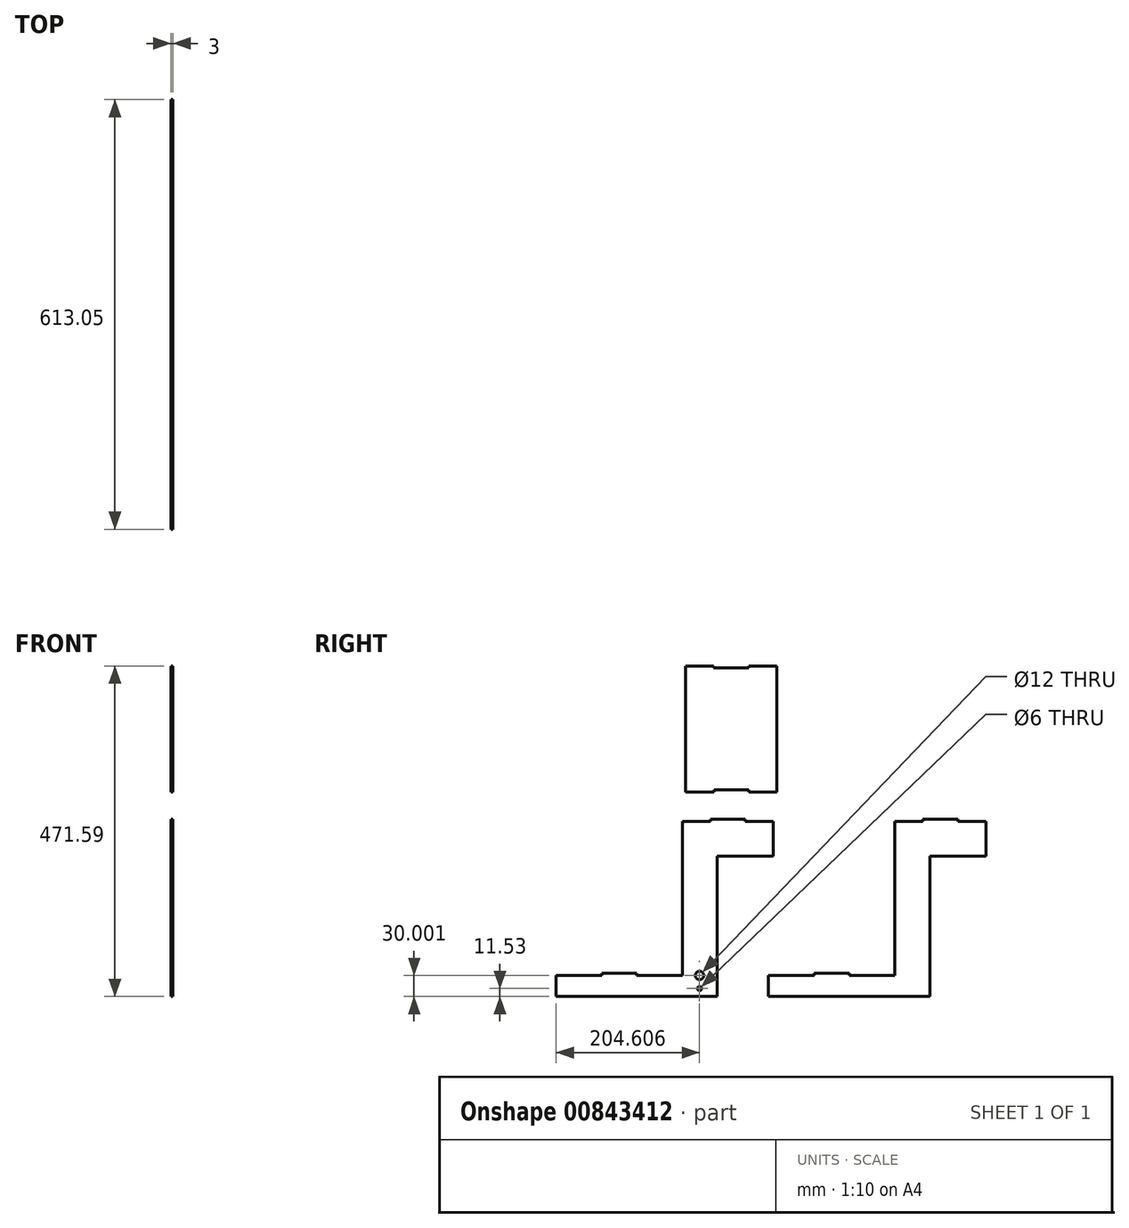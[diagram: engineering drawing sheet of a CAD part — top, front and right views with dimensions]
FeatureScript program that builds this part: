
annotation { "Feature Type Name" : "Feature", "Feature Type Description" : "" }
export const myFeature = defineFeature(function(context is Context, id is Id, definition is map)
    precondition{}
    {
        {
            var Q0;
            Q0=qCreatedBy(makeId("Right.planeOp"),FACE);
            var sketch = newSketch(context, id + "F0", { "sketchPlane" : qUnion([Q0])});
            skLineSegment(sketch, "E0", {"start": v(0, 42.16) * mm, "end": v(40, 42.16) * mm});
            skLineSegment(sketch, "E1", {"start": v(130, 42.16) * mm, "end": v(130, -7.84) * mm});
            skLineSegment(sketch, "E2", {"start": v(50, -7.84) * mm, "end": v(130, -7.84) * mm});
            skLineSegment(sketch, "E3", {"start": v(50, -7.84) * mm, "end": v(50, -207.84) * mm});
            skLineSegment(sketch, "E4", {"start": v(50, -207.84) * mm, "end": v(-180, -207.84) * mm});
            skLineSegment(sketch, "E5", {"start": v(-180, -207.84) * mm, "end": v(-180, -177.84) * mm});
            skLineSegment(sketch, "E6", {"start": v(0, -177.84) * mm, "end": v(-65, -177.84) * mm});
            skLineSegment(sketch, "E7", {"start": v(0, -177.84) * mm, "end": v(0, 42.16) * mm});
            skLineSegment(sketch, "E8", {"start": v(-298.05, 42.16) * mm, "end": v(-263.05, 42.16) * mm});
            skLineSegment(sketch, "E9", {"start": v(-173.05, 37.16) * mm, "end": v(-173.05, -2.84) * mm});
            skLineSegment(sketch, "E10", {"start": v(-248.05, -7.84) * mm, "end": v(-178.05, -7.84) * mm});
            skLineSegment(sketch, "E11", {"start": v(-253.05, -12.84) * mm, "end": v(-253.05, -207.84) * mm});
            skLineSegment(sketch, "E12", {"start": v(-253.05, -207.84) * mm, "end": v(-483.05, -207.84) * mm});
            skLineSegment(sketch, "E13", {"start": v(-483.05, -207.84) * mm, "end": v(-483.05, -177.84) * mm});
            skLineSegment(sketch, "E14", {"start": v(-303.05, -177.84) * mm, "end": v(-368.05, -177.84) * mm});
            skLineSegment(sketch, "E15", {"start": v(-303.05, -177.84) * mm, "end": v(-303.05, 37.16) * mm});
            skCircle(sketch, "E16", {"center": v(-278.44, -177.84) * mm, "radius": 6 * mm});
            skLineSegment(sketch, "E17.bottom", {"start": v(-298.36, 83.75) * mm, "end": v(-258.01, 83.75) * mm});
            skLineSegment(sketch, "E17.top", {"start": v(-298.36, 263.75) * mm, "end": v(-258.36, 263.75) * mm});
            skLineSegment(sketch, "E17.left", {"start": v(-298.36, 83.75) * mm, "end": v(-298.36, 263.75) * mm});
            skLineSegment(sketch, "E17.right", {"start": v(-168.36, 83.75) * mm, "end": v(-168.36, 263.75) * mm});
            skCircle(sketch, "E18", {"center": v(-278.44, -196.31) * mm, "radius": 3 * mm});
            skLineSegment(sketch, "E19", {"start": v(-263.05, 42.16) * mm, "end": v(-263.05, 45.16) * mm});
            skLineSegment(sketch, "E20", {"start": v(-263.05, 45.16) * mm, "end": v(-213.05, 45.16) * mm});
            skLineSegment(sketch, "E21", {"start": v(-213.05, 45.16) * mm, "end": v(-213.05, 42.16) * mm});
            skLineSegment(sketch, "E22.trimOffspring", {"start": v(-213.05, 42.16) * mm, "end": v(-178.05, 42.16) * mm});
            skLineSegment(sketch, "E23.top", {"start": v(-258.01, 86.75) * mm, "end": v(-208.01, 86.75) * mm});
            skLineSegment(sketch, "E23.left", {"start": v(-258.01, 83.75) * mm, "end": v(-258.01, 86.75) * mm});
            skLineSegment(sketch, "E23.right", {"start": v(-208.01, 83.75) * mm, "end": v(-208.01, 86.75) * mm});
            skLineSegment(sketch, "E24.trimOffspring", {"start": v(-208.01, 83.75) * mm, "end": v(-168.36, 83.75) * mm});
            skPoint(sketch, "E25.visualSharp", {"position": v(-303.05, 42.16) * mm});
            skPoint(sketch, "E26.visualSharp", {"position": v(-173.05, 42.16) * mm});
            skPoint(sketch, "E27.visualSharp", {"position": v(-173.05, -7.84) * mm});
            skPoint(sketch, "E28.visualSharp", {"position": v(-253.05, -7.84) * mm});
            skLineSegment(sketch, "E29", {"start": v(-298.05, 42.16) * mm, "end": v(-303.05, 42.16) * mm});
            skLineSegment(sketch, "E30", {"start": v(-303.05, 42.16) * mm, "end": v(-303.05, 37.16) * mm});
            skLineSegment(sketch, "E31", {"start": v(-173.05, 42.16) * mm, "end": v(-178.05, 42.16) * mm});
            skLineSegment(sketch, "E32", {"start": v(-173.05, 42.16) * mm, "end": v(-173.05, 37.16) * mm});
            skLineSegment(sketch, "E33", {"start": v(-173.05, -2.84) * mm, "end": v(-173.05, -7.84) * mm});
            skLineSegment(sketch, "E34", {"start": v(-173.05, -7.84) * mm, "end": v(-178.05, -7.84) * mm});
            skLineSegment(sketch, "E35", {"start": v(-248.05, -7.84) * mm, "end": v(-253.05, -7.84) * mm});
            skLineSegment(sketch, "E36", {"start": v(-253.05, -12.84) * mm, "end": v(-253.05, -7.84) * mm});
            skLineSegment(sketch, "E37", {"start": v(-483.05, -177.84) * mm, "end": v(-418.05, -177.84) * mm});
            skLineSegment(sketch, "E38", {"start": v(-418.05, -177.84) * mm, "end": v(-418.05, -174.84) * mm});
            skLineSegment(sketch, "E39", {"start": v(-418.05, -174.84) * mm, "end": v(-368.05, -174.84) * mm});
            skLineSegment(sketch, "E40", {"start": v(-368.05, -174.84) * mm, "end": v(-368.05, -177.84) * mm});
            skLineSegment(sketch, "E41", {"start": v(-180, -177.84) * mm, "end": v(-115, -177.84) * mm});
            skLineSegment(sketch, "E42", {"start": v(-115, -177.84) * mm, "end": v(-115, -174.84) * mm});
            skLineSegment(sketch, "E43", {"start": v(-115, -174.84) * mm, "end": v(-65, -174.84) * mm});
            skLineSegment(sketch, "E44", {"start": v(-65, -174.84) * mm, "end": v(-65, -177.84) * mm});
            skLineSegment(sketch, "E45", {"start": v(40, 42.16) * mm, "end": v(40, 45.16) * mm});
            skLineSegment(sketch, "E46", {"start": v(40, 45.16) * mm, "end": v(90, 45.16) * mm});
            skLineSegment(sketch, "E47", {"start": v(90, 45.16) * mm, "end": v(90, 42.16) * mm});
            skLineSegment(sketch, "E48.trimOffspring", {"start": v(90, 42.16) * mm, "end": v(130, 42.16) * mm});
            skLineSegment(sketch, "E49.trimOffspring", {"start": v(-115, -177.84) * mm, "end": v(-180, -177.84) * mm});
            skLineSegment(sketch, "E50.trimOffspring", {"start": v(-418.05, -177.84) * mm, "end": v(-483.05, -177.84) * mm});
            skLineSegment(sketch, "E51", {"start": v(-258.36, 263.75) * mm, "end": v(-258.36, 260.75) * mm});
            skLineSegment(sketch, "E52", {"start": v(-258.36, 260.75) * mm, "end": v(-208.36, 260.75) * mm});
            skLineSegment(sketch, "E53", {"start": v(-208.36, 260.75) * mm, "end": v(-208.36, 263.75) * mm});
            skLineSegment(sketch, "E54.trimOffspring", {"start": v(-208.36, 263.75) * mm, "end": v(-168.36, 263.75) * mm});
            skSolve(sketch);
        }
        {
            var Q0;
            Q0=makeQuery(id+"F0.imprint","IMPRINT",FACE,{"disambiguationData":[TD([[makeQuery(id+"F0.imprint","IMPRINT",EDGE,{"derivedFrom":sQuery(id+"F0.wireOp",EDGE,"E0")}),-1.0]])]});
            var Q1;
            Q1=makeQuery(id+"F0.imprint","IMPRINT",FACE,{"disambiguationData":[TD([[makeQuery(id+"F0.imprint","IMPRINT",EDGE,{"derivedFrom":sQuery(id+"F0.wireOp",EDGE,"E8")}),-1.0]])]});
            var Q2;
            Q2=makeQuery(id+"F0.imprint","IMPRINT",FACE,{"disambiguationData":[TD([[makeQuery(id+"F0.imprint","IMPRINT",EDGE,{"derivedFrom":sQuery(id+"F0.wireOp",EDGE,"E17.bottom")}),1.0]])]});
            extrude(context, id + "F1", {"entities" : qUnion([Q0, Q1, Q2]), "oppositeDirection" : true, "depth" : 3 * mm, "offsetDistance" : 25 * mm});
        }
    });
